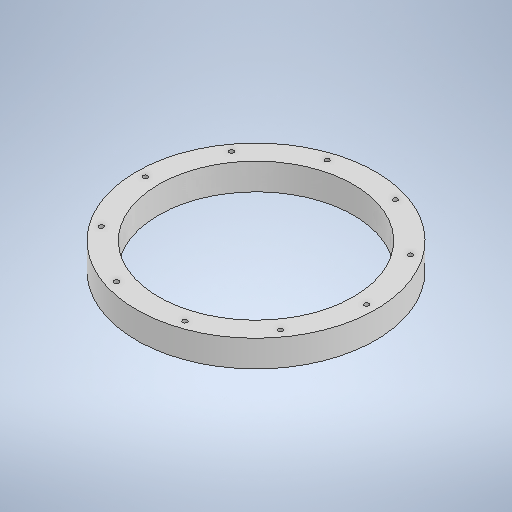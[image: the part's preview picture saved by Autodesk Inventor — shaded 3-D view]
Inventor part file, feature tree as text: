
AUTODESK INVENTOR PART (.ipt)
format: ipt  version: 2025 (Build 290162000, 162)  size: 250,880 bytes
history: native  units: in
note: dims shown in document units (in); Inventor stores cm internally (conversion verified against a paired STEP export)
features: sketch x2, extrude x1, hole x1, pattern_circular x1
ambient origin geometry x8: Origin, YZ Plane, XZ Plane, XY Plane, X Axis, Y Axis, Z Axis, Center Point
bodies: Solid1 (feature_tree)
feature tree (5):
  extrude  "Extrusion1"  Depth=8.6614in
  hole  "Hole1"  [1 undecoded]
  pattern_circular  "Circular Pattern1"  Count=10 Angle=360.0deg
  sketch  "Sketch1"  dims[d0=10.6299in d1=8.6614in]
  sketch  "Sketch2"  dims[d2=1.1811in d3=0.0in d4=0.2047in d5=0.2362in d6=0.1575in d7=0.0787in d8=90.0deg d9=0.315in d10=0.8108in d11=4.9213in d12=3.937in d13=360.0deg]
note: 1 required parameter value undecoded (feature->parameter linkage not recoverable at this tier; creation-order binding heuristic only, values carry confidence <= 0.55)
